# Revit family: 306_T-Just_ABV1-_
name_source: partatom
category: Pipe Accessories
units: mm (PartAtom-declared; Revit-internal decimal feet)

## family parameters
Always vertical = Yes
Cut with Voids When Loaded = No
Part Type = Valve - Breaks Into
Round Connector Dimension = Use Diameter
Shared = No
Work Plane-Based = No

## types (3) — shared parameters
CAT0 = Yes
Description = T-Just - Thermostatic Valve for Domestic Water
H1 = 34 mm  [stored 0.111549 ft]
H12 = 50 mm  [stored 0.164042 ft]
H1__ve = -34 mm  [stored -0.111549 ft]
L1 = 18 mm  [stored 0.0590551 ft]
L1__ve = -18 mm
L2 = 85 mm
L2D = 122 mm
L2D_Min = 3048 mm  [stored 10 ft]
L4 = 11 mm  [stored 0.0360892 ft]
L5 = 29 mm
L66 = 50 mm  [stored 0.164042 ft]
L66__ve = -50 mm  [stored -0.164042 ft]
L7 = 41 mm  [stored 0.134514 ft]
LA = 15 mm  [stored 0.0492126 ft]
LL = 61 mm  [stored 0.200131 ft]
Manufacturer = FlowCon
QmdConnectorList = 301;D;302;D
R33 = 6 mm  [stored 0.019685 ft]
RA = 13 mm  [stored 0.0426509 ft]
URL = http://flowcon.com
magiPartTypeId = 306
magiProductFamilyId = T-Just.ABV1-*
zero-valued in all types: MC_Default_elevation

## per-type parameters (varying)
| type | CenSd_RN_6 | D | H11 | L6 | L6__ve | L8 | R1 | R2 | R3 | R4 | RN | SW | W2D | magiProductId |
| T-Just.7.B-15 | 9 mm | 15 mm | 28 mm  [stored 0.0918635 ft] | 58 mm | -58 mm | 7 mm  [stored 0.0229659 ft] | 11 mm  [stored 0.0360892 ft] | 13 mm  [stored 0.0426509 ft] | 11 mm  [stored 0.0360892 ft] | 5 mm  [stored 0.0164042 ft] | 10 mm  [stored 0.0328084 ft] | 14 mm  [stored 0.0459318 ft] | 15 mm  [stored 0.0492126 ft] | T-Just.ABV1-15 |
| T-Just.7.B-25 | 11 mm  [stored 0.0360892 ft] | 25 mm | 26 mm  [stored 0.0853018 ft] | 57 mm | -57 mm | 9 mm | 14 mm  [stored 0.0459318 ft] | 16 mm  [stored 0.0524934 ft] | 14 mm  [stored 0.0459318 ft] | 7 mm  [stored 0.0229659 ft] | 13 mm  [stored 0.0426509 ft] | 18 mm  [stored 0.0590551 ft] | 25 mm  [stored 0.082021 ft] | T-Just.ABV1-25 |
| T-Just.7.B-20 | 10 mm  [stored 0.0328084 ft] | 20 mm | 27 mm | 58 mm | -58 mm | 8 mm  [stored 0.0262467 ft] | 12 mm  [stored 0.0393701 ft] | 14 mm  [stored 0.0459318 ft] | 12 mm  [stored 0.0393701 ft] | 6 mm  [stored 0.019685 ft] | 12 mm  [stored 0.0393701 ft] | 16 mm  [stored 0.0524934 ft] | 20 mm  [stored 0.0656168 ft] | T-Just.ABV1-20 |

note: column(s) folded — value = type name in every type: magiProductCode

note: [stored X ft] marks values corroborated as IEEE doubles in the binary element streams (Revit-internal decimal feet)

## geometry (parser evidence)
native form markers: Sweep x2
no freeform markers — native parametric forms only
